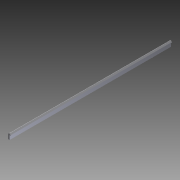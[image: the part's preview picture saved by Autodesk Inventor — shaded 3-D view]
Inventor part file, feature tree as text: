
AUTODESK INVENTOR PART (.ipt)
format: ipt  version: 2014 (Build 180170000, 170)  size: 94,208 bytes
history: native  units: in
note: dims shown in document units (in); Inventor stores cm internally (conversion verified against a paired STEP export)
features: fillet x1, other x1, imported_body x1
ambient origin geometry x8: Origin, YZ Plane, XZ Plane, XY Plane, X Axis, Y Axis, Z Axis, Center Point
bodies: Body1 (feature_tree)
feature tree (3):
  fillet  "Fillet1"  [1 undecoded]
  other  "BWC-T1-11"
  imported_body  "Base1"
note: 1 required parameter value undecoded (feature->parameter linkage not recoverable at this tier; creation-order binding heuristic only, values carry confidence <= 0.55)
